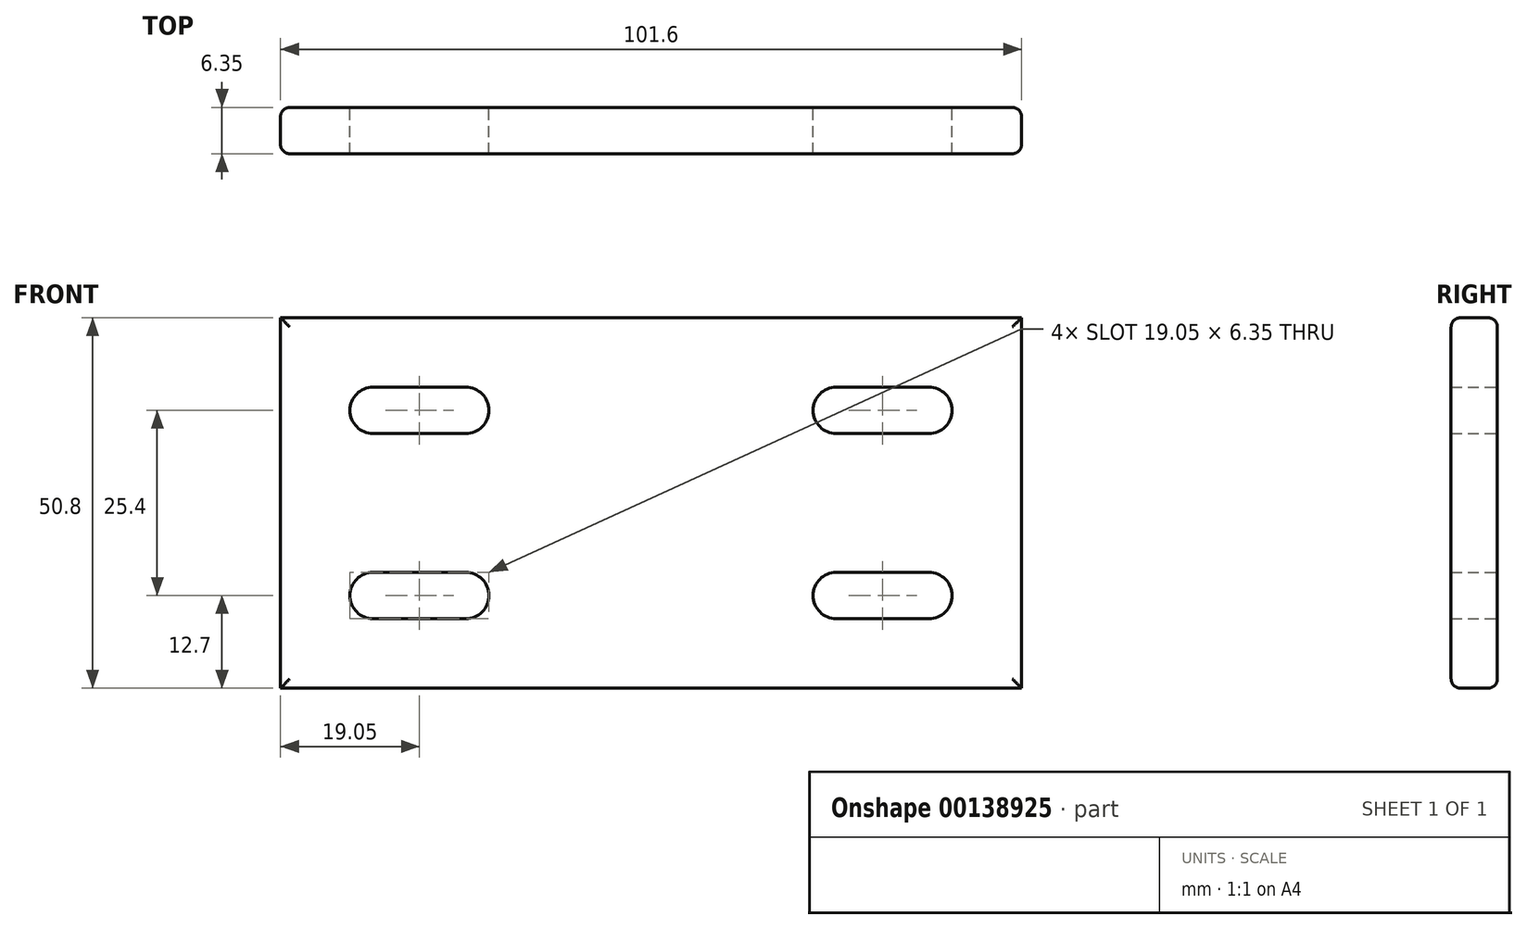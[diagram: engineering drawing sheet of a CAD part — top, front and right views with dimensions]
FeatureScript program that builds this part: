
annotation { "Feature Type Name" : "Feature", "Feature Type Description" : "" }
export const myFeature = defineFeature(function(context is Context, id is Id, definition is map)
    precondition{}
    {
        {
            var Q0;
            Q0=qCreatedBy(makeId("Front.planeOp"),FACE);
            var sketch = newSketch(context, id + "F0", { "sketchPlane" : qUnion([Q0])});
            skLineSegment(sketch, "E0.bottom", {"start": v(-50.8, 25.4) * mm, "end": v(50.8, 25.4) * mm});
            skLineSegment(sketch, "E0.top", {"start": v(-50.8, -25.4) * mm, "end": v(50.8, -25.4) * mm});
            skLineSegment(sketch, "E0.left", {"start": v(-50.8, 25.4) * mm, "end": v(-50.8, -25.4) * mm});
            skLineSegment(sketch, "E0.right", {"start": v(50.8, 25.4) * mm, "end": v(50.8, -25.4) * mm});
            skPoint(sketch, "E0.middle", {"position": v(0, 0) * mm});
            skLineSegment(sketch, "E1", {"start": v(-38.1, 12.7) * mm, "end": v(-25.4, 12.7) * mm, "construction": true});
            skArc(sketch, "E2.0.startCap", {"start": v(-38.1, 9.53) * mm, "mid": v(-41.27, 12.7) * mm, "end": v(-38.1, 15.88) * mm});
            skArc(sketch, "E2.0.endCap", {"start": v(-25.4, 15.88) * mm, "mid": v(-22.22, 12.7) * mm, "end": v(-25.4, 9.53) * mm});
            skLineSegment(sketch, "E2.0.left", {"start": v(-38.1, 15.88) * mm, "end": v(-25.4, 15.88) * mm});
            skLineSegment(sketch, "E2.0.right", {"start": v(-38.1, 9.53) * mm, "end": v(-25.4, 9.53) * mm});
            skLineSegment(sketch, "E3", {"start": v(-50.8, 0) * mm, "end": v(50.8, 0) * mm, "construction": true});
            skLineSegment(sketch, "E4", {"start": v(0, 25.4) * mm, "end": v(0, -25.4) * mm, "construction": true});
            skLineSegment(sketch, "E5.MirrorCS", {"start": v(-38.1, -12.7) * mm, "end": v(-25.4, -12.7) * mm, "construction": true});
            skLineSegment(sketch, "E6.MirrorCS", {"start": v(-38.1, -15.88) * mm, "end": v(-25.4, -15.88) * mm});
            skLineSegment(sketch, "E7.MirrorCS", {"start": v(-38.1, -9.53) * mm, "end": v(-25.4, -9.53) * mm});
            skArc(sketch, "E8.MirrorCS", {"start": v(-25.4, -15.88) * mm, "mid": v(-22.22, -12.7) * mm, "end": v(-25.4, -9.53) * mm});
            skArc(sketch, "E9.MirrorCS", {"start": v(-38.1, -9.53) * mm, "mid": v(-41.27, -12.7) * mm, "end": v(-38.1, -15.88) * mm});
            skLineSegment(sketch, "E10.MirrorCS", {"start": v(38.1, 15.88) * mm, "end": v(25.4, 15.88) * mm});
            skLineSegment(sketch, "E11.MirrorCS", {"start": v(38.1, 9.53) * mm, "end": v(25.4, 9.53) * mm});
            skArc(sketch, "E12.MirrorCS", {"start": v(25.4, 15.88) * mm, "mid": v(22.23, 12.7) * mm, "end": v(25.4, 9.53) * mm});
            skArc(sketch, "E13.MirrorCS", {"start": v(38.1, 9.52) * mm, "mid": v(41.28, 12.7) * mm, "end": v(38.1, 15.87) * mm});
            skLineSegment(sketch, "E14.MirrorCS", {"start": v(38.1, -9.53) * mm, "end": v(25.4, -9.53) * mm});
            skArc(sketch, "E15.MirrorCS", {"start": v(38.1, -9.53) * mm, "mid": v(41.27, -12.7) * mm, "end": v(38.1, -15.88) * mm});
            skLineSegment(sketch, "E16.MirrorCS", {"start": v(38.1, -15.88) * mm, "end": v(25.4, -15.88) * mm});
            skArc(sketch, "E17.MirrorCS", {"start": v(25.4, -15.88) * mm, "mid": v(22.22, -12.7) * mm, "end": v(25.4, -9.53) * mm});
            skSolve(sketch);
        }
        {
            var Q0;
            Q0=makeQuery(id+"F0.imprint","IMPRINT",FACE,{"disambiguationData":[TD([[makeQuery(id+"F0.imprint","IMPRINT",EDGE,{"derivedFrom":sQuery(id+"F0.wireOp",EDGE,"E0.bottom")}),-1.0]])]});
            extrude(context, id + "F1", {"entities" : qUnion([Q0]), "depth" : 6.35 * mm});
        }
        {
            var Q0;
            Q0=makeQuery(id+"F1.opExtrude","CAP_EDGE",EDGE,{"disambiguationData":[OSD([sQuery(id+"F0.wireOp",EDGE,"E0.top")])],"isStart":true});
            var Q1;
            Q1=makeQuery(id+"F1.opExtrude","CAP_EDGE",EDGE,{"disambiguationData":[OSD([sQuery(id+"F0.wireOp",EDGE,"E0.left")])],"isStart":true});
            var Q2;
            Q2=makeQuery(id+"F1.opExtrude","CAP_EDGE",EDGE,{"disambiguationData":[OSD([sQuery(id+"F0.wireOp",EDGE,"E0.right")])],"isStart":true});
            var Q3;
            Q3=makeQuery(id+"F1.opExtrude","CAP_EDGE",EDGE,{"disambiguationData":[OSD([sQuery(id+"F0.wireOp",EDGE,"E0.bottom")])],"isStart":true});
            var Q4;
            Q4=makeQuery(id+"F1.opExtrude","CAP_EDGE",EDGE,{"disambiguationData":[OSD([sQuery(id+"F0.wireOp",EDGE,"E0.bottom")])],"isStart":false});
            var Q5;
            Q5=makeQuery(id+"F1.opExtrude","CAP_EDGE",EDGE,{"disambiguationData":[OSD([sQuery(id+"F0.wireOp",EDGE,"E0.left")])],"isStart":false});
            var Q6;
            Q6=makeQuery(id+"F1.opExtrude","CAP_EDGE",EDGE,{"disambiguationData":[OSD([sQuery(id+"F0.wireOp",EDGE,"E0.right")])],"isStart":false});
            var Q7;
            Q7=makeQuery(id+"F1.opExtrude","CAP_EDGE",EDGE,{"disambiguationData":[OSD([sQuery(id+"F0.wireOp",EDGE,"E0.top")])],"isStart":false});
            fillet(context, id + "F2", {"entities" : qUnion([Q0, Q1, Q2, Q3, Q4, Q5, Q6, Q7]), "radius" : 1.27 * mm, "tangentPropagation" : true, "allowEdgeOverflow" : false});
        }
    });
